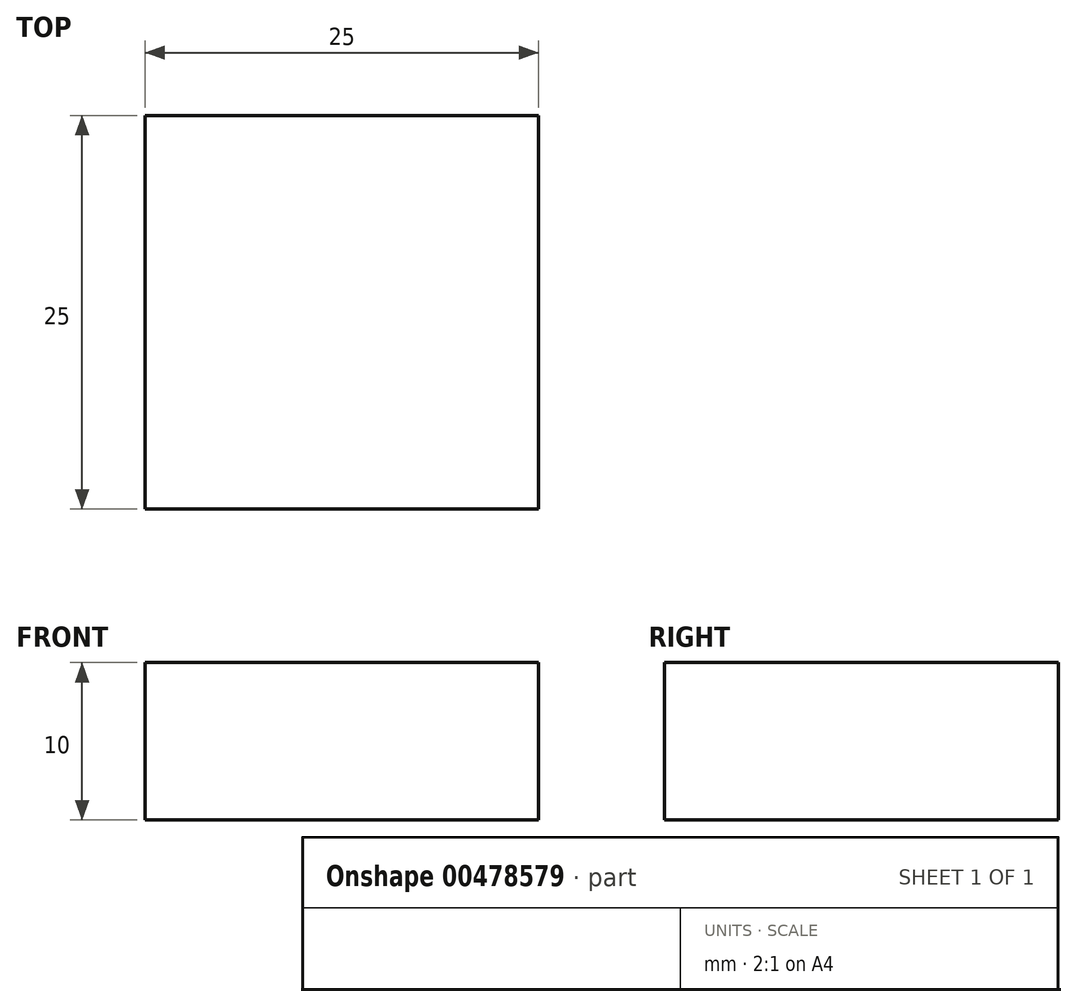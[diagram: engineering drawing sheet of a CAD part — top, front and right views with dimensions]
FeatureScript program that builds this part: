
annotation { "Feature Type Name" : "Feature", "Feature Type Description" : "" }
export const myFeature = defineFeature(function(context is Context, id is Id, definition is map)
    precondition{}
    {
        {
            var Q0;
            Q0=qCreatedBy(makeId("Top.planeOp"),FACE);
            var sketch = newSketch(context, id + "F0", { "sketchPlane" : qUnion([Q0])});
            skLineSegment(sketch, "E0.bottom", {"start": v(0, 0) * mm, "end": v(25, 0) * mm});
            skLineSegment(sketch, "E0.top", {"start": v(0, 25) * mm, "end": v(25, 25) * mm});
            skLineSegment(sketch, "E0.left", {"start": v(0, 0) * mm, "end": v(0, 25) * mm});
            skLineSegment(sketch, "E0.right", {"start": v(25, 0) * mm, "end": v(25, 25) * mm});
            skSolve(sketch);
        }
        {
            var Q0;
            Q0 = qSketchRegion(id + "F0", true);
            extrude(context, id + "F1", {"entities" : qUnion([Q0]), "depth" : 10 * mm, "offsetDistance" : 25 * mm});
        }
    });
